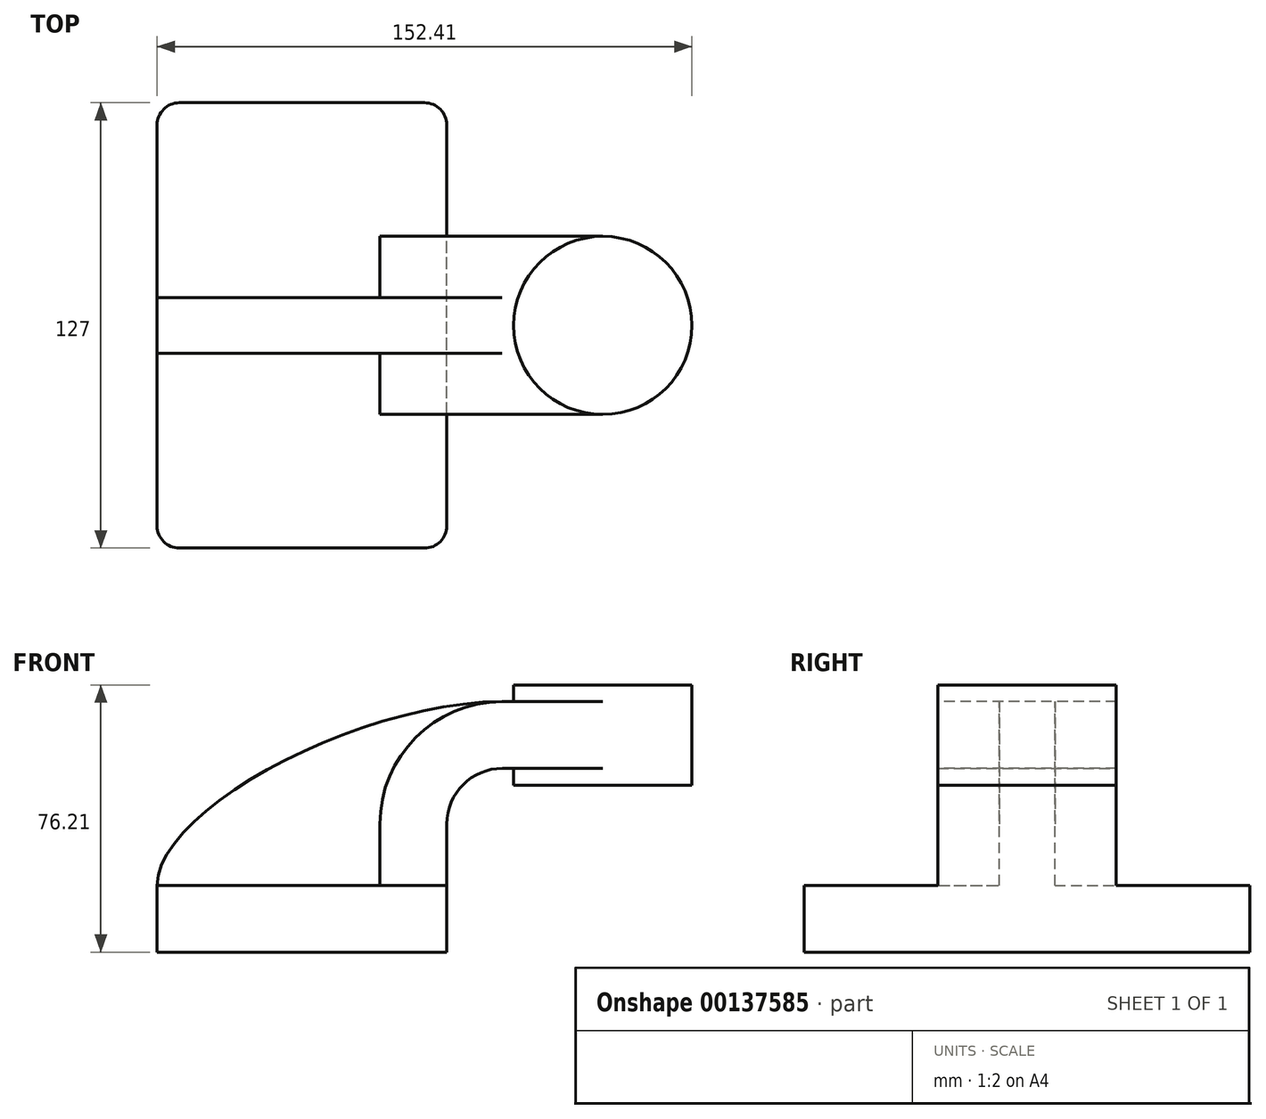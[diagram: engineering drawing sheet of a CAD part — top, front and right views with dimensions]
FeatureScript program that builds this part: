
annotation { "Feature Type Name" : "Feature", "Feature Type Description" : "" }
export const myFeature = defineFeature(function(context is Context, id is Id, definition is map)
    precondition{}
    {
        {
            var Q0;
            Q0=qCreatedBy(makeId("Front.planeOp"),FACE);
            var sketch = newSketch(context, id + "F0", { "sketchPlane" : qUnion([Q0])});
            skLineSegment(sketch, "E0.bottom", {"start": v(-41.28, 9.52) * mm, "end": v(41.27, 9.53) * mm});
            skLineSegment(sketch, "E0.top", {"start": v(-41.28, -9.53) * mm, "end": v(41.28, -9.53) * mm});
            skLineSegment(sketch, "E0.left", {"start": v(-41.28, 9.52) * mm, "end": v(-41.27, -9.53) * mm});
            skLineSegment(sketch, "E0.right", {"start": v(41.28, 9.53) * mm, "end": v(41.28, -9.52) * mm});
            skPoint(sketch, "E0.middle", {"position": v(0, 0) * mm});
            skLineSegment(sketch, "E1.bottom", {"start": v(111.12, 38.1) * mm, "end": v(60.32, 38.1) * mm});
            skLineSegment(sketch, "E1.top", {"start": v(111.12, 66.67) * mm, "end": v(60.32, 66.67) * mm});
            skLineSegment(sketch, "E1.left", {"start": v(111.12, 38.1) * mm, "end": v(111.12, 66.67) * mm});
            skLineSegment(sketch, "E1.right", {"start": v(60.32, 38.1) * mm, "end": v(60.32, 66.68) * mm});
            skPoint(sketch, "E1.middle", {"position": v(85.72, 52.39) * mm});
            skLineSegment(sketch, "E2", {"start": v(41.27, 9.53) * mm, "end": v(41.27, 27) * mm});
            skArc(sketch, "E3", {"start": v(41.27, 27) * mm, "mid": v(45.92, 38.23) * mm, "end": v(57.15, 42.88) * mm});
            skLineSegment(sketch, "E4", {"start": v(57.15, 42.88) * mm, "end": v(85.72, 42.88) * mm});
            skLineSegment(sketch, "E5.0", {"start": v(57.15, 61.93) * mm, "end": v(85.73, 61.93) * mm});
            skArc(sketch, "E5.1", {"start": v(22.23, 27) * mm, "mid": v(32.45, 51.7) * mm, "end": v(57.15, 61.93) * mm});
            skLineSegment(sketch, "E5.2", {"start": v(22.22, 9.53) * mm, "end": v(22.22, 27) * mm});
            skLineSegment(sketch, "E6", {"start": v(85.73, 66.67) * mm, "end": v(85.72, 38.1) * mm});
            skFitSpline(sketch, "E7", {"points": [v(-41.28, 9.52) * mm, v(57.15, 61.93) * mm], "startDerivative": vector(0.54, 65.48) * mm, "endDerivative": vector(122.61, 0.22) * mm});
            skSolve(sketch);
        }
        {
            var Q0;
            Q0=makeQuery(id+"F0.imprint","IMPRINT",FACE,{"disambiguationData":[TD([[makeQuery(id+"F0.imprint","IMPRINT",EDGE,{"derivedFrom":sQuery(id+"F0.wireOp",EDGE,"E0.top")}),1.0]])]});
            extrude(context, id + "F1", {"entities" : qUnion([Q0]), "endBound" : BoundingType.SYMMETRIC, "depth" : 127 * mm});
        }
        {
            var Q0;
            {var subQ1=sQuery(id+"F0.wireOp",EDGE,"E2");Q0=makeQuery(id+"F0.imprint","IMPRINT",FACE,{"disambiguationData":[TD([[makeQuery(id+"F0.imprint","IMPRINT",EDGE,{"derivedFrom":subQ1}),1.0]])]});}
            extrude(context, id + "F2", {"entities" : qUnion([Q0]), "operationType" : NewBodyOperationType.ADD, "endBound" : BoundingType.SYMMETRIC, "depth" : 50.8 * mm});
        }
        {
            var Q0;
            {var subQ3=sQuery(id+"F0.wireOp",EDGE,"E5.2");Q0=makeQuery(id+"F0.imprint","IMPRINT",FACE,{"disambiguationData":[TD([[makeQuery(id+"F0.imprint","IMPRINT",EDGE,{"derivedFrom":subQ3}),1.0]])]});}
            extrude(context, id + "F3", {"entities" : qUnion([Q0]), "operationType" : NewBodyOperationType.ADD, "endBound" : BoundingType.SYMMETRIC, "depth" : 15.88 * mm});
        }
        {
            var Q0;
            {var subQ0=sQuery(id+"F0.wireOp",EDGE,"E4");var subQ1=sQuery(id+"F0.wireOp",EDGE,"E1.right");var subQ2=makeQuery(id+"F0.imprint","INTERSECT",VERTEX,{"derivedFrom":[subQ1,subQ0]});Q0=makeQuery(id+"F0.imprint","IMPRINT",FACE,{"disambiguationData":[TD([[makeQuery(id+"F0.imprint","IMPRINT",EDGE,{"disambiguationData":[TD([[subQ2,-1.0]])],"derivedFrom":subQ1}),-1.0]])]});}
            extrude(context, id + "F4", {"entities" : qUnion([Q0]), "operationType" : NewBodyOperationType.ADD, "endBound" : BoundingType.SYMMETRIC, "depth" : 50.8 * mm});
        }
        {
            var Q0;
            {var subQ0=sQuery(id+"F0.wireOp",EDGE,"E1.left");Q0=makeQuery(id+"F0.imprint","IMPRINT",FACE,{"disambiguationData":[TD([[makeQuery(id+"F0.imprint","IMPRINT",EDGE,{"derivedFrom":subQ0}),1.0]])]});}
            var Q1;
            Q1=sQuery(id+"F0.wireOp",EDGE,"E6");
            revolve(context, id + "F5", {"operationType" : NewBodyOperationType.ADD, "entities" : qUnion([Q0]), "axis" : qUnion([Q1]), "revolveType" : RevolveType.FULL});
        }
        {
            var Q0;
            Q0=makeQuery(id+"F1.opExtrude","CAP_EDGE",EDGE,{"disambiguationData":[OSD([sQuery(id+"F0.wireOp",EDGE,"E0.left")])],"isStart":false});
            var Q1;
            Q1=makeQuery(id+"F1.opExtrude","CAP_EDGE",EDGE,{"disambiguationData":[OSD([sQuery(id+"F0.wireOp",EDGE,"E0.right")])],"isStart":false});
            var Q2;
            Q2=makeQuery(id+"F1.opExtrude","CAP_EDGE",EDGE,{"disambiguationData":[OSD([sQuery(id+"F0.wireOp",EDGE,"E0.right")])],"isStart":true});
            var Q3;
            Q3=makeQuery(id+"F1.opExtrude","CAP_EDGE",EDGE,{"disambiguationData":[OSD([sQuery(id+"F0.wireOp",EDGE,"E0.left")])],"isStart":true});
            fillet(context, id + "F6", {"entities" : qUnion([Q0, Q1, Q2, Q3]), "radius" : 6.35 * mm, "tangentPropagation" : true, "allowEdgeOverflow" : false});
        }
    });
